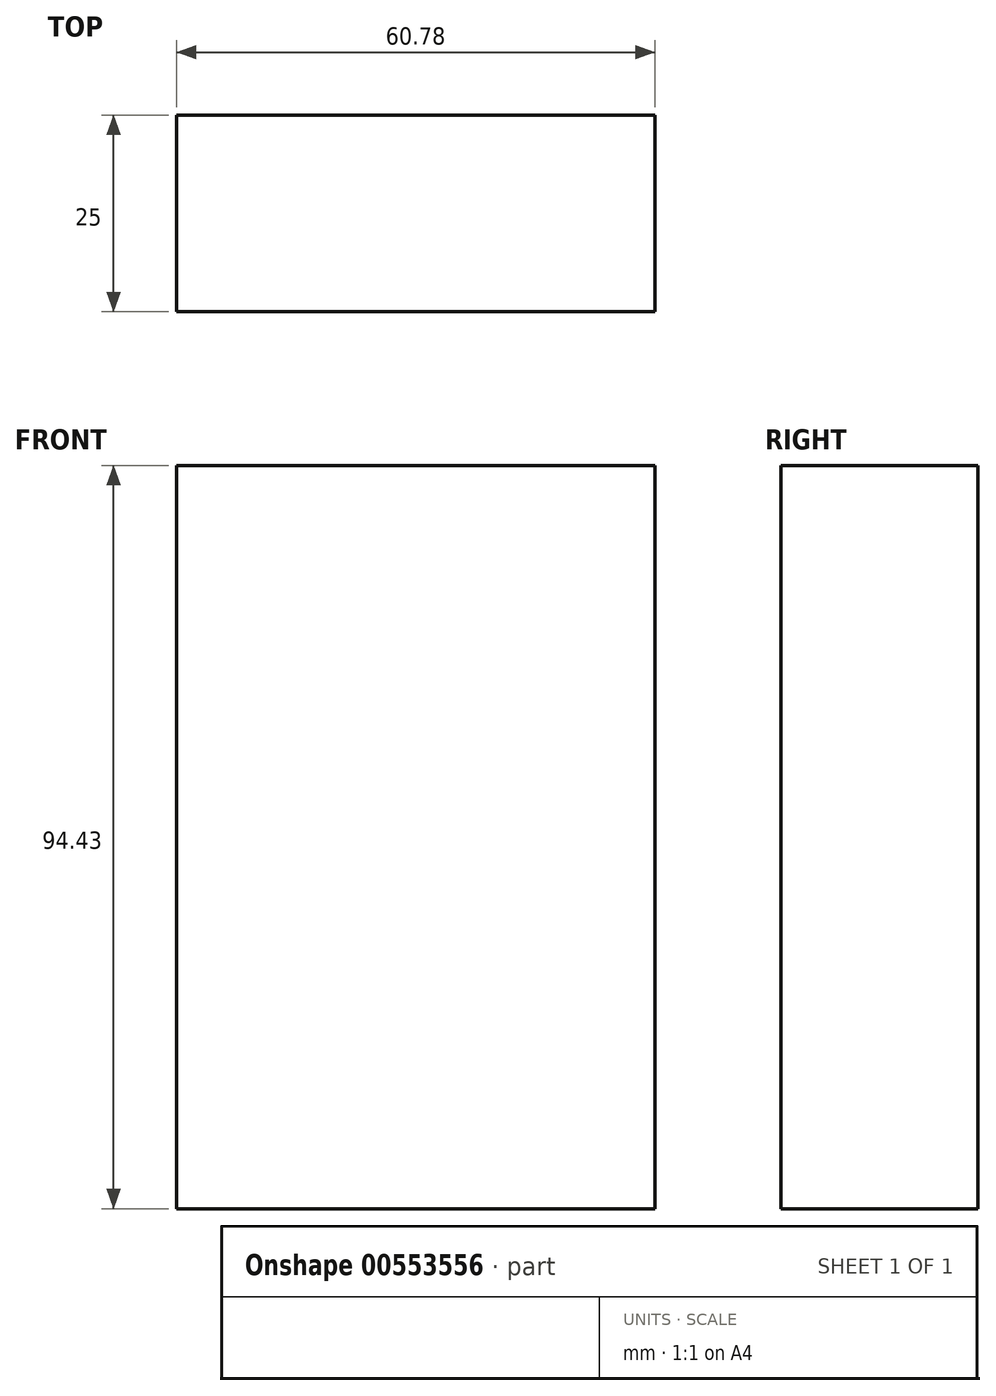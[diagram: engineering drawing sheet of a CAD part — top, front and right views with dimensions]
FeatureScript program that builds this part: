
annotation { "Feature Type Name" : "Feature", "Feature Type Description" : "" }
export const myFeature = defineFeature(function(context is Context, id is Id, definition is map)
    precondition{}
    {
        {
            var Q0;
            Q0=qCreatedBy(makeId("Front.planeOp"),FACE);
            var sketch = newSketch(context, id + "F0", { "sketchPlane" : qUnion([Q0])});
            skLineSegment(sketch, "E0.bottom", {"start": v(-138.1, 120.14) * mm, "end": v(-77.32, 120.14) * mm});
            skLineSegment(sketch, "E0.top", {"start": v(-138.1, 25.71) * mm, "end": v(-77.32, 25.71) * mm});
            skLineSegment(sketch, "E0.left", {"start": v(-138.1, 120.14) * mm, "end": v(-138.1, 25.71) * mm});
            skLineSegment(sketch, "E0.right", {"start": v(-77.32, 120.14) * mm, "end": v(-77.32, 25.71) * mm});
            skSolve(sketch);
        }
        {
            var Q0;
            Q0 = qSketchRegion(id + "F0", true);
            extrude(context, id + "F1", {"entities" : qUnion([Q0]), "depth" : 25 * mm, "offsetDistance" : 25 * mm});
        }
    });
